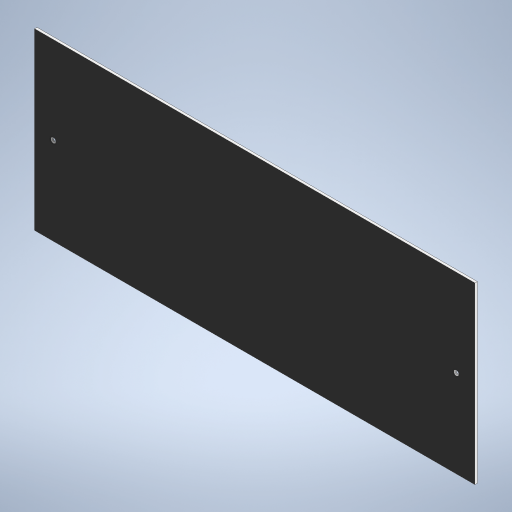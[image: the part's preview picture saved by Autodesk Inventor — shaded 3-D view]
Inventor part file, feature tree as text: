
AUTODESK INVENTOR PART (.ipt)
format: ipt  version: 2023 (Build 270158000, 158)  size: 214,016 bytes
history: native  units: mm
features: sketch x2, extrude x1, hole x1
ambient origin geometry x8: Origin, YZ Plane, XZ Plane, XY Plane, X Axis, Y Axis, Z Axis, Center Point
bodies: Solid1 (feature_tree)
feature tree (4):
  extrude  "Extrusion1"  Depth=215.0mm
  hole  "Hole1"  [1 undecoded]
  sketch  "Sketch1"  dims[d0=542.0mm d1=215.0mm]
  sketch  "Sketch2"  dims[d2=3.0mm d3=0.0mm d4=23.0mm d5=23.0mm d6=6.5mm d7=6.0mm d8=4.0mm d9=2.0mm d10=90.0deg d11=8.0mm d12=20.594885mm]
note: 1 required parameter value undecoded (feature->parameter linkage not recoverable at this tier; creation-order binding heuristic only, values carry confidence <= 0.55)
